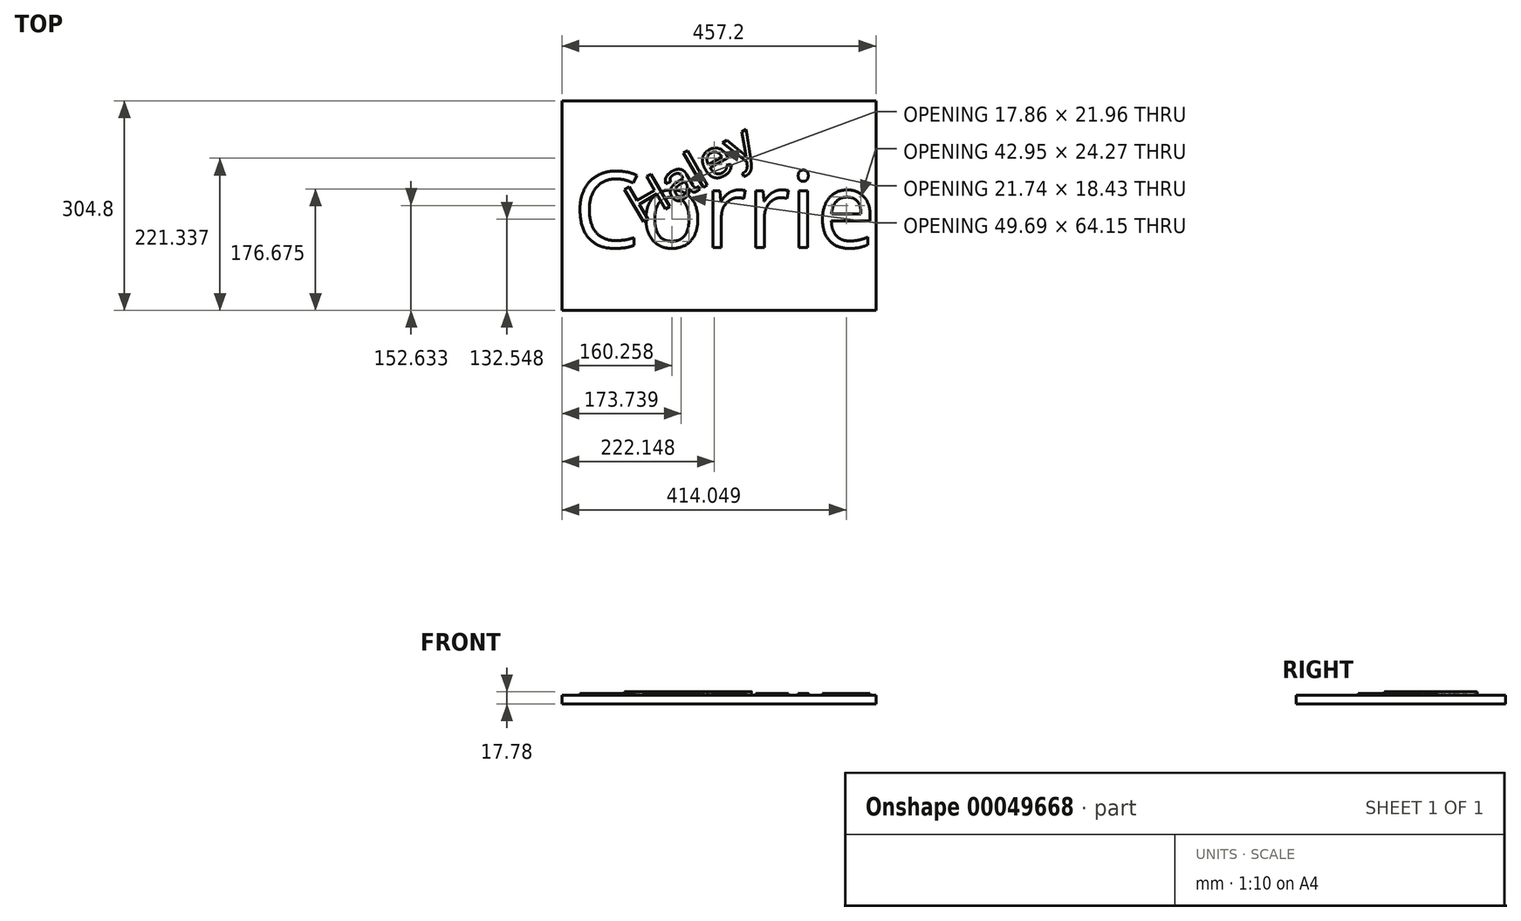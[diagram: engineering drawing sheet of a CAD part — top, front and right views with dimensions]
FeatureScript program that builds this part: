
annotation { "Feature Type Name" : "Feature", "Feature Type Description" : "" }
export const myFeature = defineFeature(function(context is Context, id is Id, definition is map)
    precondition{}
    {
        {
            var Q0;
            Q0=qCreatedBy(makeId("Top.planeOp"),FACE);
            var sketch = newSketch(context, id + "F0", { "sketchPlane" : qUnion([Q0])});
            skText(sketch, "E0", { "text": "Corrie", "fontName": "OpenSans-Regular.ttf"});
            const initialGuessF0  = {"E0": [-0.08454, -0.0511, 1, 0, 0.11051]};
            skSetInitialGuess(sketch, initialGuessF0);
            skSolve(sketch);
        }
        {
            var Q0;
            Q0 = qSketchRegion(id + "F0", true);
            extrude(context, id + "F1", {"entities" : qUnion([Q0]), "depth" : 2.54 * mm});
        }
        {
            var Q0;
            Q0=qCreatedBy(makeId("Top.planeOp"),FACE);
            var sketch = newSketch(context, id + "F2", { "sketchPlane" : qUnion([Q0])});
            skLineSegment(sketch, "E1.bottom", {"start": v(0, 162.15) * mm, "end": v(457.2, 162.15) * mm});
            skLineSegment(sketch, "E1.top", {"start": v(0, -142.65) * mm, "end": v(457.2, -142.65) * mm});
            skLineSegment(sketch, "E1.left", {"start": v(0, 162.15) * mm, "end": v(0, -142.65) * mm});
            skLineSegment(sketch, "E1.right", {"start": v(457.2, 162.15) * mm, "end": v(457.2, -142.65) * mm});
            skSolve(sketch);
        }
        {
            var Q0;
            Q0=makeQuery(id+"F2.imprint","IMPRINT",FACE,{"disambiguationData":[TD([[makeQuery(id+"F2.imprint","IMPRINT",EDGE,{"derivedFrom":sQuery(id+"F2.wireOp",EDGE,"E1.bottom")}),-1.0]])]});
            extrude(context, id + "F3", {"entities" : qUnion([Q0]), "depth" : 12.7 * mm});
        }
        {
            var Q0;
            Q0=makeQuery(id+"F1.opExtrude","SWEPT_BODY",BODY,{"disambiguationData":[OSD([sQuery(id+"F0.wireOp",EDGE,"E0.sketch_text.stroke-0"),sQuery(id+"F0.wireOp",EDGE,"E0.sketch_text.stroke-1"),sQuery(id+"F0.wireOp",EDGE,"E0.sketch_text.stroke-2"),sQuery(id+"F0.wireOp",EDGE,"E0.sketch_text.stroke-3"),sQuery(id+"F0.wireOp",EDGE,"E0.sketch_text.stroke-4"),sQuery(id+"F0.wireOp",EDGE,"E0.sketch_text.stroke-5"),sQuery(id+"F0.wireOp",EDGE,"E0.sketch_text.stroke-6"),sQuery(id+"F0.wireOp",EDGE,"E0.sketch_text.stroke-7"),sQuery(id+"F0.wireOp",EDGE,"E0.sketch_text.stroke-8"),sQuery(id+"F0.wireOp",EDGE,"E0.sketch_text.stroke-9"),sQuery(id+"F0.wireOp",EDGE,"E0.sketch_text.stroke-10"),sQuery(id+"F0.wireOp",EDGE,"E0.sketch_text.stroke-11"),sQuery(id+"F0.wireOp",EDGE,"E0.sketch_text.stroke-12"),sQuery(id+"F0.wireOp",EDGE,"E0.sketch_text.stroke-13"),sQuery(id+"F0.wireOp",EDGE,"E0.sketch_text.stroke-14")])]});
            var Q1;
            Q1=makeQuery(id+"F1.opExtrude","SWEPT_BODY",BODY,{"disambiguationData":[OSD([sQuery(id+"F0.wireOp",EDGE,"E0.sketch_text.stroke-15"),sQuery(id+"F0.wireOp",EDGE,"E0.sketch_text.stroke-16"),sQuery(id+"F0.wireOp",EDGE,"E0.sketch_text.stroke-17"),sQuery(id+"F0.wireOp",EDGE,"E0.sketch_text.stroke-18"),sQuery(id+"F0.wireOp",EDGE,"E0.sketch_text.stroke-19"),sQuery(id+"F0.wireOp",EDGE,"E0.sketch_text.stroke-20"),sQuery(id+"F0.wireOp",EDGE,"E0.sketch_text.stroke-21"),sQuery(id+"F0.wireOp",EDGE,"E0.sketch_text.stroke-22"),sQuery(id+"F0.wireOp",EDGE,"E0.sketch_text.stroke-23"),sQuery(id+"F0.wireOp",EDGE,"E0.sketch_text.stroke-24"),sQuery(id+"F0.wireOp",EDGE,"E0.sketch_text.stroke-25"),sQuery(id+"F0.wireOp",EDGE,"E0.sketch_text.stroke-26"),sQuery(id+"F0.wireOp",EDGE,"E0.sketch_text.stroke-27"),sQuery(id+"F0.wireOp",EDGE,"E0.sketch_text.stroke-28"),sQuery(id+"F0.wireOp",EDGE,"E0.sketch_text.stroke-29"),sQuery(id+"F0.wireOp",EDGE,"E0.sketch_text.stroke-30"),sQuery(id+"F0.wireOp",EDGE,"E0.sketch_text.stroke-31")])]});
            var Q2;
            Q2=makeQuery(id+"F1.opExtrude","SWEPT_BODY",BODY,{"disambiguationData":[OSD([sQuery(id+"F0.wireOp",EDGE,"E0.sketch_text.stroke-32"),sQuery(id+"F0.wireOp",EDGE,"E0.sketch_text.stroke-33"),sQuery(id+"F0.wireOp",EDGE,"E0.sketch_text.stroke-34"),sQuery(id+"F0.wireOp",EDGE,"E0.sketch_text.stroke-35"),sQuery(id+"F0.wireOp",EDGE,"E0.sketch_text.stroke-36"),sQuery(id+"F0.wireOp",EDGE,"E0.sketch_text.stroke-37"),sQuery(id+"F0.wireOp",EDGE,"E0.sketch_text.stroke-38"),sQuery(id+"F0.wireOp",EDGE,"E0.sketch_text.stroke-39"),sQuery(id+"F0.wireOp",EDGE,"E0.sketch_text.stroke-40"),sQuery(id+"F0.wireOp",EDGE,"E0.sketch_text.stroke-41"),sQuery(id+"F0.wireOp",EDGE,"E0.sketch_text.stroke-42"),sQuery(id+"F0.wireOp",EDGE,"E0.sketch_text.stroke-43"),sQuery(id+"F0.wireOp",EDGE,"E0.sketch_text.stroke-44")])]});
            var Q3;
            Q3=makeQuery(id+"F1.opExtrude","SWEPT_BODY",BODY,{"disambiguationData":[OSD([sQuery(id+"F0.wireOp",EDGE,"E0.sketch_text.stroke-45"),sQuery(id+"F0.wireOp",EDGE,"E0.sketch_text.stroke-46"),sQuery(id+"F0.wireOp",EDGE,"E0.sketch_text.stroke-47"),sQuery(id+"F0.wireOp",EDGE,"E0.sketch_text.stroke-48"),sQuery(id+"F0.wireOp",EDGE,"E0.sketch_text.stroke-49"),sQuery(id+"F0.wireOp",EDGE,"E0.sketch_text.stroke-50"),sQuery(id+"F0.wireOp",EDGE,"E0.sketch_text.stroke-51"),sQuery(id+"F0.wireOp",EDGE,"E0.sketch_text.stroke-52"),sQuery(id+"F0.wireOp",EDGE,"E0.sketch_text.stroke-53"),sQuery(id+"F0.wireOp",EDGE,"E0.sketch_text.stroke-54"),sQuery(id+"F0.wireOp",EDGE,"E0.sketch_text.stroke-55"),sQuery(id+"F0.wireOp",EDGE,"E0.sketch_text.stroke-56"),sQuery(id+"F0.wireOp",EDGE,"E0.sketch_text.stroke-57")])]});
            var Q4;
            Q4=makeQuery(id+"F1.opExtrude","SWEPT_BODY",BODY,{"disambiguationData":[OSD([sQuery(id+"F0.wireOp",EDGE,"E0.sketch_text.stroke-58"),sQuery(id+"F0.wireOp",EDGE,"E0.sketch_text.stroke-59"),sQuery(id+"F0.wireOp",EDGE,"E0.sketch_text.stroke-60"),sQuery(id+"F0.wireOp",EDGE,"E0.sketch_text.stroke-61")])]});
            var Q5;
            Q5=makeQuery(id+"F1.opExtrude","SWEPT_BODY",BODY,{"disambiguationData":[OSD([sQuery(id+"F0.wireOp",EDGE,"E0.sketch_text.stroke-62"),sQuery(id+"F0.wireOp",EDGE,"E0.sketch_text.stroke-63"),sQuery(id+"F0.wireOp",EDGE,"E0.sketch_text.stroke-64"),sQuery(id+"F0.wireOp",EDGE,"E0.sketch_text.stroke-65"),sQuery(id+"F0.wireOp",EDGE,"E0.sketch_text.stroke-66"),sQuery(id+"F0.wireOp",EDGE,"E0.sketch_text.stroke-67"),sQuery(id+"F0.wireOp",EDGE,"E0.sketch_text.stroke-68"),sQuery(id+"F0.wireOp",EDGE,"E0.sketch_text.stroke-69")])]});
            var Q6;
            Q6=makeQuery(id+"F1.opExtrude","SWEPT_BODY",BODY,{"disambiguationData":[OSD([sQuery(id+"F0.wireOp",EDGE,"E0.sketch_text.stroke-70"),sQuery(id+"F0.wireOp",EDGE,"E0.sketch_text.stroke-71"),sQuery(id+"F0.wireOp",EDGE,"E0.sketch_text.stroke-72"),sQuery(id+"F0.wireOp",EDGE,"E0.sketch_text.stroke-73"),sQuery(id+"F0.wireOp",EDGE,"E0.sketch_text.stroke-74"),sQuery(id+"F0.wireOp",EDGE,"E0.sketch_text.stroke-75"),sQuery(id+"F0.wireOp",EDGE,"E0.sketch_text.stroke-76"),sQuery(id+"F0.wireOp",EDGE,"E0.sketch_text.stroke-77"),sQuery(id+"F0.wireOp",EDGE,"E0.sketch_text.stroke-78"),sQuery(id+"F0.wireOp",EDGE,"E0.sketch_text.stroke-79"),sQuery(id+"F0.wireOp",EDGE,"E0.sketch_text.stroke-80"),sQuery(id+"F0.wireOp",EDGE,"E0.sketch_text.stroke-81"),sQuery(id+"F0.wireOp",EDGE,"E0.sketch_text.stroke-82"),sQuery(id+"F0.wireOp",EDGE,"E0.sketch_text.stroke-83"),sQuery(id+"F0.wireOp",EDGE,"E0.sketch_text.stroke-84"),sQuery(id+"F0.wireOp",EDGE,"E0.sketch_text.stroke-85"),sQuery(id+"F0.wireOp",EDGE,"E0.sketch_text.stroke-86"),sQuery(id+"F0.wireOp",EDGE,"E0.sketch_text.stroke-87"),sQuery(id+"F0.wireOp",EDGE,"E0.sketch_text.stroke-88")])]});
            transform(context, id + "F4", {"entities" : qUnion([Q0, Q1, Q2, Q3, Q4, Q5, Q6]), "transformType" : TransformType.TRANSLATION_3D, "dx" : 101.6 * mm, "dy" : 0 * mm, "dz" : 12.7 * mm, "makeCopy" : false});
        }
        {
            var Q0;
            Q0=qCreatedBy(makeId("Top.planeOp"),FACE);
            var sketch = newSketch(context, id + "F5", { "sketchPlane" : qUnion([Q0])});
            skText(sketch, "E2", { "text": "Haley", "fontName": "Arimo-Regular.ttf"});
            const initialGuessF5  = {"E2": [0.0083, -0.01433, 1, 0, 0.05727]};
            skSetInitialGuess(sketch, initialGuessF5);
            skSolve(sketch);
        }
        {
            var Q0;
            Q0 = qSketchRegion(id + "F5", true);
            extrude(context, id + "F6", {"entities" : qUnion([Q0]), "depth" : 5.08 * mm});
        }
        {
            var Q0;
            Q0=makeQuery(id+"F6.opExtrude","SWEPT_BODY",BODY,{"disambiguationData":[OSD([sQuery(id+"F5.wireOp",EDGE,"E2.sketch_text.stroke-0"),sQuery(id+"F5.wireOp",EDGE,"E2.sketch_text.stroke-1"),sQuery(id+"F5.wireOp",EDGE,"E2.sketch_text.stroke-2"),sQuery(id+"F5.wireOp",EDGE,"E2.sketch_text.stroke-3"),sQuery(id+"F5.wireOp",EDGE,"E2.sketch_text.stroke-4"),sQuery(id+"F5.wireOp",EDGE,"E2.sketch_text.stroke-5"),sQuery(id+"F5.wireOp",EDGE,"E2.sketch_text.stroke-6"),sQuery(id+"F5.wireOp",EDGE,"E2.sketch_text.stroke-7"),sQuery(id+"F5.wireOp",EDGE,"E2.sketch_text.stroke-8"),sQuery(id+"F5.wireOp",EDGE,"E2.sketch_text.stroke-9"),sQuery(id+"F5.wireOp",EDGE,"E2.sketch_text.stroke-10"),sQuery(id+"F5.wireOp",EDGE,"E2.sketch_text.stroke-11")])]});
            var Q1;
            Q1=makeQuery(id+"F6.opExtrude","SWEPT_BODY",BODY,{"disambiguationData":[OSD([sQuery(id+"F5.wireOp",EDGE,"E2.sketch_text.stroke-12"),sQuery(id+"F5.wireOp",EDGE,"E2.sketch_text.stroke-13"),sQuery(id+"F5.wireOp",EDGE,"E2.sketch_text.stroke-14"),sQuery(id+"F5.wireOp",EDGE,"E2.sketch_text.stroke-15"),sQuery(id+"F5.wireOp",EDGE,"E2.sketch_text.stroke-16"),sQuery(id+"F5.wireOp",EDGE,"E2.sketch_text.stroke-17"),sQuery(id+"F5.wireOp",EDGE,"E2.sketch_text.stroke-18"),sQuery(id+"F5.wireOp",EDGE,"E2.sketch_text.stroke-19"),sQuery(id+"F5.wireOp",EDGE,"E2.sketch_text.stroke-20"),sQuery(id+"F5.wireOp",EDGE,"E2.sketch_text.stroke-21"),sQuery(id+"F5.wireOp",EDGE,"E2.sketch_text.stroke-22"),sQuery(id+"F5.wireOp",EDGE,"E2.sketch_text.stroke-23"),sQuery(id+"F5.wireOp",EDGE,"E2.sketch_text.stroke-24"),sQuery(id+"F5.wireOp",EDGE,"E2.sketch_text.stroke-25"),sQuery(id+"F5.wireOp",EDGE,"E2.sketch_text.stroke-26"),sQuery(id+"F5.wireOp",EDGE,"E2.sketch_text.stroke-27"),sQuery(id+"F5.wireOp",EDGE,"E2.sketch_text.stroke-28"),sQuery(id+"F5.wireOp",EDGE,"E2.sketch_text.stroke-29"),sQuery(id+"F5.wireOp",EDGE,"E2.sketch_text.stroke-30"),sQuery(id+"F5.wireOp",EDGE,"E2.sketch_text.stroke-31"),sQuery(id+"F5.wireOp",EDGE,"E2.sketch_text.stroke-32"),sQuery(id+"F5.wireOp",EDGE,"E2.sketch_text.stroke-33"),sQuery(id+"F5.wireOp",EDGE,"E2.sketch_text.stroke-34"),sQuery(id+"F5.wireOp",EDGE,"E2.sketch_text.stroke-35"),sQuery(id+"F5.wireOp",EDGE,"E2.sketch_text.stroke-36"),sQuery(id+"F5.wireOp",EDGE,"E2.sketch_text.stroke-37"),sQuery(id+"F5.wireOp",EDGE,"E2.sketch_text.stroke-38"),sQuery(id+"F5.wireOp",EDGE,"E2.sketch_text.stroke-39"),sQuery(id+"F5.wireOp",EDGE,"E2.sketch_text.stroke-40"),sQuery(id+"F5.wireOp",EDGE,"E2.sketch_text.stroke-41"),sQuery(id+"F5.wireOp",EDGE,"E2.sketch_text.stroke-42"),sQuery(id+"F5.wireOp",EDGE,"E2.sketch_text.stroke-43"),sQuery(id+"F5.wireOp",EDGE,"E2.sketch_text.stroke-44"),sQuery(id+"F5.wireOp",EDGE,"E2.sketch_text.stroke-45"),sQuery(id+"F5.wireOp",EDGE,"E2.sketch_text.stroke-46")])]});
            var Q2;
            Q2=makeQuery(id+"F6.opExtrude","SWEPT_BODY",BODY,{"disambiguationData":[OSD([sQuery(id+"F5.wireOp",EDGE,"E2.sketch_text.stroke-47"),sQuery(id+"F5.wireOp",EDGE,"E2.sketch_text.stroke-48"),sQuery(id+"F5.wireOp",EDGE,"E2.sketch_text.stroke-49"),sQuery(id+"F5.wireOp",EDGE,"E2.sketch_text.stroke-50")])]});
            var Q3;
            Q3=makeQuery(id+"F6.opExtrude","SWEPT_BODY",BODY,{"disambiguationData":[OSD([sQuery(id+"F5.wireOp",EDGE,"E2.sketch_text.stroke-51"),sQuery(id+"F5.wireOp",EDGE,"E2.sketch_text.stroke-52"),sQuery(id+"F5.wireOp",EDGE,"E2.sketch_text.stroke-53"),sQuery(id+"F5.wireOp",EDGE,"E2.sketch_text.stroke-54"),sQuery(id+"F5.wireOp",EDGE,"E2.sketch_text.stroke-55"),sQuery(id+"F5.wireOp",EDGE,"E2.sketch_text.stroke-56"),sQuery(id+"F5.wireOp",EDGE,"E2.sketch_text.stroke-57"),sQuery(id+"F5.wireOp",EDGE,"E2.sketch_text.stroke-58"),sQuery(id+"F5.wireOp",EDGE,"E2.sketch_text.stroke-59"),sQuery(id+"F5.wireOp",EDGE,"E2.sketch_text.stroke-60"),sQuery(id+"F5.wireOp",EDGE,"E2.sketch_text.stroke-61"),sQuery(id+"F5.wireOp",EDGE,"E2.sketch_text.stroke-62"),sQuery(id+"F5.wireOp",EDGE,"E2.sketch_text.stroke-63"),sQuery(id+"F5.wireOp",EDGE,"E2.sketch_text.stroke-64"),sQuery(id+"F5.wireOp",EDGE,"E2.sketch_text.stroke-65"),sQuery(id+"F5.wireOp",EDGE,"E2.sketch_text.stroke-66"),sQuery(id+"F5.wireOp",EDGE,"E2.sketch_text.stroke-67"),sQuery(id+"F5.wireOp",EDGE,"E2.sketch_text.stroke-68")])]});
            var Q4;
            Q4=makeQuery(id+"F6.opExtrude","SWEPT_BODY",BODY,{"disambiguationData":[OSD([sQuery(id+"F5.wireOp",EDGE,"E2.sketch_text.stroke-69"),sQuery(id+"F5.wireOp",EDGE,"E2.sketch_text.stroke-70"),sQuery(id+"F5.wireOp",EDGE,"E2.sketch_text.stroke-71"),sQuery(id+"F5.wireOp",EDGE,"E2.sketch_text.stroke-72"),sQuery(id+"F5.wireOp",EDGE,"E2.sketch_text.stroke-73"),sQuery(id+"F5.wireOp",EDGE,"E2.sketch_text.stroke-74"),sQuery(id+"F5.wireOp",EDGE,"E2.sketch_text.stroke-75"),sQuery(id+"F5.wireOp",EDGE,"E2.sketch_text.stroke-76"),sQuery(id+"F5.wireOp",EDGE,"E2.sketch_text.stroke-77"),sQuery(id+"F5.wireOp",EDGE,"E2.sketch_text.stroke-78"),sQuery(id+"F5.wireOp",EDGE,"E2.sketch_text.stroke-79"),sQuery(id+"F5.wireOp",EDGE,"E2.sketch_text.stroke-80"),sQuery(id+"F5.wireOp",EDGE,"E2.sketch_text.stroke-81"),sQuery(id+"F5.wireOp",EDGE,"E2.sketch_text.stroke-82"),sQuery(id+"F5.wireOp",EDGE,"E2.sketch_text.stroke-83"),sQuery(id+"F5.wireOp",EDGE,"E2.sketch_text.stroke-84"),sQuery(id+"F5.wireOp",EDGE,"E2.sketch_text.stroke-85"),sQuery(id+"F5.wireOp",EDGE,"E2.sketch_text.stroke-86")])]});
            transform(context, id + "F7", {"entities" : qUnion([Q0, Q1, Q2, Q3, Q4]), "transformType" : TransformType.TRANSLATION_3D, "dx" : 152.4 * mm, "dy" : -76.2 * mm, "dz" : 12.7 * mm, "makeCopy" : false});
        }
        {
            var Q0;
            Q0=makeQuery(id+"F6.opExtrude","SWEPT_BODY",BODY,{"disambiguationData":[OSD([sQuery(id+"F5.wireOp",EDGE,"E2.sketch_text.stroke-0"),sQuery(id+"F5.wireOp",EDGE,"E2.sketch_text.stroke-1"),sQuery(id+"F5.wireOp",EDGE,"E2.sketch_text.stroke-2"),sQuery(id+"F5.wireOp",EDGE,"E2.sketch_text.stroke-3"),sQuery(id+"F5.wireOp",EDGE,"E2.sketch_text.stroke-4"),sQuery(id+"F5.wireOp",EDGE,"E2.sketch_text.stroke-5"),sQuery(id+"F5.wireOp",EDGE,"E2.sketch_text.stroke-6"),sQuery(id+"F5.wireOp",EDGE,"E2.sketch_text.stroke-7"),sQuery(id+"F5.wireOp",EDGE,"E2.sketch_text.stroke-8"),sQuery(id+"F5.wireOp",EDGE,"E2.sketch_text.stroke-9"),sQuery(id+"F5.wireOp",EDGE,"E2.sketch_text.stroke-10"),sQuery(id+"F5.wireOp",EDGE,"E2.sketch_text.stroke-11")])]});
            var Q1;
            Q1=makeQuery(id+"F6.opExtrude","SWEPT_BODY",BODY,{"disambiguationData":[OSD([sQuery(id+"F5.wireOp",EDGE,"E2.sketch_text.stroke-12"),sQuery(id+"F5.wireOp",EDGE,"E2.sketch_text.stroke-13"),sQuery(id+"F5.wireOp",EDGE,"E2.sketch_text.stroke-14"),sQuery(id+"F5.wireOp",EDGE,"E2.sketch_text.stroke-15"),sQuery(id+"F5.wireOp",EDGE,"E2.sketch_text.stroke-16"),sQuery(id+"F5.wireOp",EDGE,"E2.sketch_text.stroke-17"),sQuery(id+"F5.wireOp",EDGE,"E2.sketch_text.stroke-18"),sQuery(id+"F5.wireOp",EDGE,"E2.sketch_text.stroke-19"),sQuery(id+"F5.wireOp",EDGE,"E2.sketch_text.stroke-20"),sQuery(id+"F5.wireOp",EDGE,"E2.sketch_text.stroke-21"),sQuery(id+"F5.wireOp",EDGE,"E2.sketch_text.stroke-22"),sQuery(id+"F5.wireOp",EDGE,"E2.sketch_text.stroke-23"),sQuery(id+"F5.wireOp",EDGE,"E2.sketch_text.stroke-24"),sQuery(id+"F5.wireOp",EDGE,"E2.sketch_text.stroke-25"),sQuery(id+"F5.wireOp",EDGE,"E2.sketch_text.stroke-26"),sQuery(id+"F5.wireOp",EDGE,"E2.sketch_text.stroke-27"),sQuery(id+"F5.wireOp",EDGE,"E2.sketch_text.stroke-28"),sQuery(id+"F5.wireOp",EDGE,"E2.sketch_text.stroke-29"),sQuery(id+"F5.wireOp",EDGE,"E2.sketch_text.stroke-30"),sQuery(id+"F5.wireOp",EDGE,"E2.sketch_text.stroke-31"),sQuery(id+"F5.wireOp",EDGE,"E2.sketch_text.stroke-32"),sQuery(id+"F5.wireOp",EDGE,"E2.sketch_text.stroke-33"),sQuery(id+"F5.wireOp",EDGE,"E2.sketch_text.stroke-34"),sQuery(id+"F5.wireOp",EDGE,"E2.sketch_text.stroke-35"),sQuery(id+"F5.wireOp",EDGE,"E2.sketch_text.stroke-36"),sQuery(id+"F5.wireOp",EDGE,"E2.sketch_text.stroke-37"),sQuery(id+"F5.wireOp",EDGE,"E2.sketch_text.stroke-38"),sQuery(id+"F5.wireOp",EDGE,"E2.sketch_text.stroke-39"),sQuery(id+"F5.wireOp",EDGE,"E2.sketch_text.stroke-40"),sQuery(id+"F5.wireOp",EDGE,"E2.sketch_text.stroke-41"),sQuery(id+"F5.wireOp",EDGE,"E2.sketch_text.stroke-42"),sQuery(id+"F5.wireOp",EDGE,"E2.sketch_text.stroke-43"),sQuery(id+"F5.wireOp",EDGE,"E2.sketch_text.stroke-44"),sQuery(id+"F5.wireOp",EDGE,"E2.sketch_text.stroke-45"),sQuery(id+"F5.wireOp",EDGE,"E2.sketch_text.stroke-46")])]});
            var Q2;
            Q2=makeQuery(id+"F6.opExtrude","SWEPT_BODY",BODY,{"disambiguationData":[OSD([sQuery(id+"F5.wireOp",EDGE,"E2.sketch_text.stroke-47"),sQuery(id+"F5.wireOp",EDGE,"E2.sketch_text.stroke-48"),sQuery(id+"F5.wireOp",EDGE,"E2.sketch_text.stroke-49"),sQuery(id+"F5.wireOp",EDGE,"E2.sketch_text.stroke-50")])]});
            var Q3;
            Q3=makeQuery(id+"F6.opExtrude","SWEPT_BODY",BODY,{"disambiguationData":[OSD([sQuery(id+"F5.wireOp",EDGE,"E2.sketch_text.stroke-51"),sQuery(id+"F5.wireOp",EDGE,"E2.sketch_text.stroke-52"),sQuery(id+"F5.wireOp",EDGE,"E2.sketch_text.stroke-53"),sQuery(id+"F5.wireOp",EDGE,"E2.sketch_text.stroke-54"),sQuery(id+"F5.wireOp",EDGE,"E2.sketch_text.stroke-55"),sQuery(id+"F5.wireOp",EDGE,"E2.sketch_text.stroke-56"),sQuery(id+"F5.wireOp",EDGE,"E2.sketch_text.stroke-57"),sQuery(id+"F5.wireOp",EDGE,"E2.sketch_text.stroke-58"),sQuery(id+"F5.wireOp",EDGE,"E2.sketch_text.stroke-59"),sQuery(id+"F5.wireOp",EDGE,"E2.sketch_text.stroke-60"),sQuery(id+"F5.wireOp",EDGE,"E2.sketch_text.stroke-61"),sQuery(id+"F5.wireOp",EDGE,"E2.sketch_text.stroke-62"),sQuery(id+"F5.wireOp",EDGE,"E2.sketch_text.stroke-63"),sQuery(id+"F5.wireOp",EDGE,"E2.sketch_text.stroke-64"),sQuery(id+"F5.wireOp",EDGE,"E2.sketch_text.stroke-65"),sQuery(id+"F5.wireOp",EDGE,"E2.sketch_text.stroke-66"),sQuery(id+"F5.wireOp",EDGE,"E2.sketch_text.stroke-67"),sQuery(id+"F5.wireOp",EDGE,"E2.sketch_text.stroke-68")])]});
            var Q4;
            Q4=makeQuery(id+"F6.opExtrude","SWEPT_BODY",BODY,{"disambiguationData":[OSD([sQuery(id+"F5.wireOp",EDGE,"E2.sketch_text.stroke-69"),sQuery(id+"F5.wireOp",EDGE,"E2.sketch_text.stroke-70"),sQuery(id+"F5.wireOp",EDGE,"E2.sketch_text.stroke-71"),sQuery(id+"F5.wireOp",EDGE,"E2.sketch_text.stroke-72"),sQuery(id+"F5.wireOp",EDGE,"E2.sketch_text.stroke-73"),sQuery(id+"F5.wireOp",EDGE,"E2.sketch_text.stroke-74"),sQuery(id+"F5.wireOp",EDGE,"E2.sketch_text.stroke-75"),sQuery(id+"F5.wireOp",EDGE,"E2.sketch_text.stroke-76"),sQuery(id+"F5.wireOp",EDGE,"E2.sketch_text.stroke-77"),sQuery(id+"F5.wireOp",EDGE,"E2.sketch_text.stroke-78"),sQuery(id+"F5.wireOp",EDGE,"E2.sketch_text.stroke-79"),sQuery(id+"F5.wireOp",EDGE,"E2.sketch_text.stroke-80"),sQuery(id+"F5.wireOp",EDGE,"E2.sketch_text.stroke-81"),sQuery(id+"F5.wireOp",EDGE,"E2.sketch_text.stroke-82"),sQuery(id+"F5.wireOp",EDGE,"E2.sketch_text.stroke-83"),sQuery(id+"F5.wireOp",EDGE,"E2.sketch_text.stroke-84"),sQuery(id+"F5.wireOp",EDGE,"E2.sketch_text.stroke-85"),sQuery(id+"F5.wireOp",EDGE,"E2.sketch_text.stroke-86")])]});
            var Q5;
            Q5=makeQuery(id+"F3.opExtrude","SWEPT_EDGE",EDGE,{"disambiguationData":[OSD([sQuery(id+"F2.wireOp",EDGE,"E1.top"),sQuery(id+"F2.wireOp",EDGE,"E1.left")])]});
            transform(context, id + "F8", {"entities" : qUnion([Q0, Q1, Q2, Q3, Q4]), "transformType" : TransformType.ROTATION, "transformAxis" : qUnion([Q5]), "angle" : 330 * degree, "makeCopy" : false});
        }
    });
